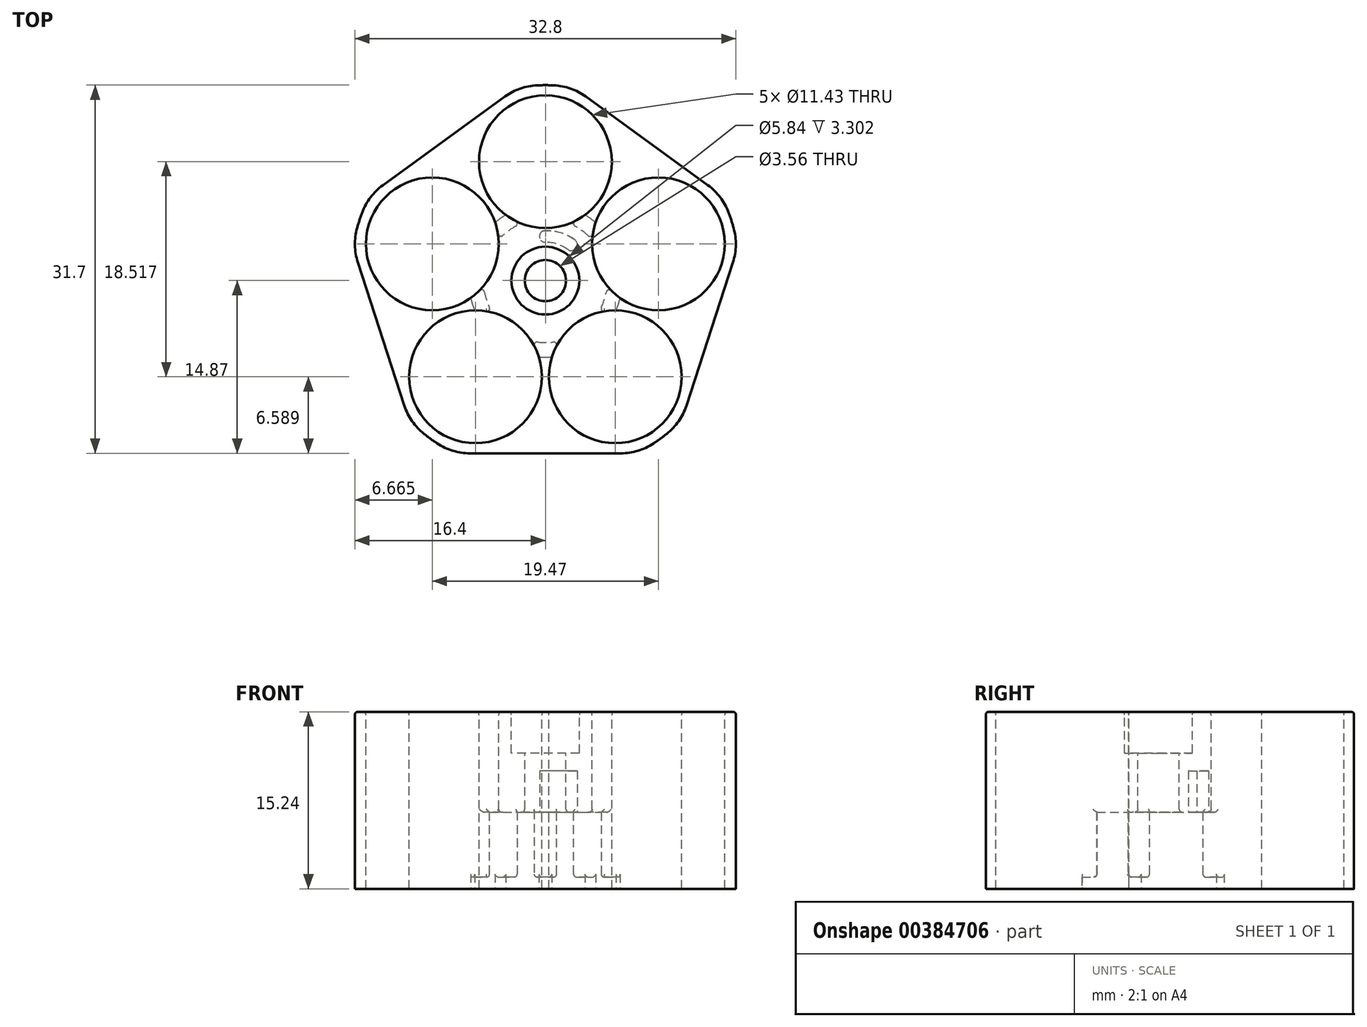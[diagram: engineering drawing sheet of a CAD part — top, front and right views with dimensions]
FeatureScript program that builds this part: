
annotation { "Feature Type Name" : "Feature", "Feature Type Description" : "" }
export const myFeature = defineFeature(function(context is Context, id is Id, definition is map)
    precondition{}
    {
        {
            var Q0;
            Q0=qCreatedBy(makeId("Top.planeOp"),FACE);
            var sketch = newSketch(context, id + "F0", { "sketchPlane" : qUnion([Q0])});
            skCircle(sketch, "E0", {"center": v(0, 0) * mm, "radius": 16.83 * mm});
            skSolve(sketch);
        }
        {
            var Q0;
            Q0=qSketchRegion(id+"F0",true);
            extrude(context, id + "F1", {"entities" : qUnion([Q0]), "depth" : 15.24 * mm, "offsetDistance" : 25.4 * mm});
        }
        {
            var Q0;
            Q0=makeQuery(id+"F1.opExtrude","CAP_FACE",FACE,{"disambiguationData":[OSD([sQuery(id+"F0.wireOp",EDGE,"E0")])],"isStart":false});
            var sketch = newSketch(context, id + "F2", { "sketchPlane" : qUnion([Q0])});
            skCircle(sketch, "E1", {"center": v(0, 10.24) * mm, "radius": 5.72 * mm});
            skCircle(sketch, "E2.1.0", {"center": v(-9.74, 3.16) * mm, "radius": 5.72 * mm});
            skCircle(sketch, "E2.2.0", {"center": v(-6.02, -8.28) * mm, "radius": 5.72 * mm});
            skCircle(sketch, "E2.3.0", {"center": v(6.02, -8.28) * mm, "radius": 5.72 * mm});
            skCircle(sketch, "E2.4.0", {"center": v(9.74, 3.16) * mm, "radius": 5.72 * mm});
            skPoint(sketch, "E2.center", {"position": v(0, 0) * mm});
            skSolve(sketch);
        }
        {
            var Q0;
            Q0=qSketchRegion(id+"F2",true);
            extrude(context, id + "F3", {"entities" : qUnion([Q0]), "operationType" : NewBodyOperationType.REMOVE, "oppositeDirection" : true, "depth" : 15.24 * mm});
        }
        {
            var Q0;
            Q0=makeQuery(id+"F1.opExtrude","CAP_FACE",FACE,{"disambiguationData":[OSD([sQuery(id+"F0.wireOp",EDGE,"E0")])],"isStart":true});
            var sketch = newSketch(context, id + "F4", { "sketchPlane" : qUnion([Q0])});
            skCircle(sketch, "E3", {"center": v(0, 0) * mm, "radius": 5.33 * mm});
            skSolve(sketch);
        }
        {
            var Q0;
            Q0=qSketchRegion(id+"F4",true);
            extrude(context, id + "F5", {"entities" : qUnion([Q0]), "operationType" : NewBodyOperationType.REMOVE, "oppositeDirection" : true, "depth" : 6.6 * mm, "offsetDistance" : 25.4 * mm});
        }
        {
            var Q0;
            Q0=makeQuery(id+"F1.opExtrude","CAP_FACE",FACE,{"disambiguationData":[OSD([sQuery(id+"F0.wireOp",EDGE,"E0")])],"isStart":false});
            var sketch = newSketch(context, id + "F6", { "sketchPlane" : qUnion([Q0])});
            skCircle(sketch, "E4", {"center": v(0, 0) * mm, "radius": 2.92 * mm});
            skSolve(sketch);
        }
        {
            var Q0;
            Q0=qSketchRegion(id+"F6",true);
            extrude(context, id + "F7", {"entities" : qUnion([Q0]), "operationType" : NewBodyOperationType.REMOVE, "oppositeDirection" : true, "depth" : 3.56 * mm});
        }
        {
            var Q0;
            Q0=makeQuery(id+"F7.boolean.opBoolean","COPY",FACE,{"derivedFrom":makeQuery(id+"F7.opExtrude","CAP_FACE",FACE,{"disambiguationData":[OSD([sQuery(id+"F6.wireOp",EDGE,"E4")])],"isStart":false})});
            var sketch = newSketch(context, id + "F8", { "sketchPlane" : qUnion([Q0])});
            skCircle(sketch, "E5", {"center": v(0, 0) * mm, "radius": 1.78 * mm});
            skSolve(sketch);
        }
        {
            var Q0;
            Q0=qSketchRegion(id+"F8",true);
            extrude(context, id + "F9", {"entities" : qUnion([Q0]), "operationType" : NewBodyOperationType.REMOVE, "oppositeDirection" : true, "depth" : 25.4 * mm});
        }
        {
            var Q0;
            Q0=makeQuery(id+"F1.opExtrude","CAP_FACE",FACE,{"disambiguationData":[OSD([sQuery(id+"F0.wireOp",EDGE,"E0")])],"isStart":true});
            var sketch = newSketch(context, id + "F10", { "sketchPlane" : qUnion([Q0])});
            skSolve(sketch);
        }
        {
            var Q0;
            {var subQ0=sQuery(id+"F0.wireOp",EDGE,"E0");Q0=makeQuery(id+"F10.imprint","IMPRINT",FACE,{"disambiguationData":[TD([[makeQuery(id+"F10.imprint","IMPRINT",EDGE,{"derivedFrom":makeQuery(id+"F1.opExtrude","CAP_EDGE",EDGE,{"disambiguationData":[OSD([subQ0])],"isStart":true})}),-1.0]])]});}
            var sketch = newSketch(context, id + "F11", { "sketchPlane" : qUnion([Q0])});
            skCircle(sketch, "E6", {"center": v(0, 0) * mm, "radius": 6.6 * mm});
            skSolve(sketch);
        }
        {
            var Q0;
            Q0=qSketchRegion(id+"F11",true);
            extrude(context, id + "F12", {"entities" : qUnion([Q0]), "operationType" : NewBodyOperationType.REMOVE, "oppositeDirection" : true, "depth" : 1.02 * mm, "offsetDistance" : 25.4 * mm});
        }
        {
            var Q0;
            Q0=qCreatedBy(makeId("Top.planeOp"),FACE);
            var sketch = newSketch(context, id + "F13", { "sketchPlane" : qUnion([Q0])});
            skArc(sketch, "E7", {"start": v(0, 4.32) * mm, "mid": v(-0.5, 3.81) * mm, "end": v(0, 3.3) * mm});
            skArc(sketch, "E8", {"start": v(1.94, 2.67) * mm, "mid": v(2.65, 2.78) * mm, "end": v(2.54, 3.5) * mm});
            skArc(sketch, "E9", {"start": v(1.94, 2.67) * mm, "mid": v(1.02, 3.14) * mm, "end": v(0, 3.3) * mm});
            skArc(sketch, "E10", {"start": v(2.54, 3.5) * mm, "mid": v(1.33, 4.1) * mm, "end": v(0, 4.32) * mm});
            skPoint(sketch, "E11.trimOffspring.end.orphan", {"position": v(6.02, -8.28) * mm});
            skSolve(sketch);
        }
        {
            var Q0;
            Q0=qSketchRegion(id+"F13",true);
            extrude(context, id + "F14", {"entities" : qUnion([Q0]), "operationType" : NewBodyOperationType.REMOVE, "depth" : 10.16 * mm, "offsetDistance" : 25.4 * mm});
        }
        {
            var Q0;
            Q0=makeQuery(id+"F5.boolean.opBoolean","INTERSECT",EDGE,{"disambiguationData":[OD(0.0)],"derivedFrom":[makeQuery(id+"F3.boolean.opBoolean","COPY",FACE,{"derivedFrom":makeQuery(id+"F3.opExtrude","SWEPT_FACE",FACE,{"disambiguationData":[OSD([sQuery(id+"F2.wireOp",EDGE,"E2.3.0")])]})}),makeQuery(id+"F5.opExtrude","SWEPT_FACE",FACE,{"disambiguationData":[OSD([sQuery(id+"F4.wireOp",EDGE,"E3")])]})]});
            var Q1;
            Q1=makeQuery(id+"F5.boolean.opBoolean","INTERSECT",EDGE,{"disambiguationData":[OD(1.0)],"derivedFrom":[makeQuery(id+"F3.boolean.opBoolean","COPY",FACE,{"derivedFrom":makeQuery(id+"F3.opExtrude","SWEPT_FACE",FACE,{"disambiguationData":[OSD([sQuery(id+"F2.wireOp",EDGE,"E2.2.0")])]})}),makeQuery(id+"F5.opExtrude","SWEPT_FACE",FACE,{"disambiguationData":[OSD([sQuery(id+"F4.wireOp",EDGE,"E3")])]})]});
            var Q2;
            Q2=makeQuery(id+"F5.boolean.opBoolean","INTERSECT",EDGE,{"disambiguationData":[OD(0.0)],"derivedFrom":[makeQuery(id+"F3.boolean.opBoolean","COPY",FACE,{"derivedFrom":makeQuery(id+"F3.opExtrude","SWEPT_FACE",FACE,{"disambiguationData":[OSD([sQuery(id+"F2.wireOp",EDGE,"E2.2.0")])]})}),makeQuery(id+"F5.opExtrude","SWEPT_FACE",FACE,{"disambiguationData":[OSD([sQuery(id+"F4.wireOp",EDGE,"E3")])]})]});
            var Q3;
            Q3=makeQuery(id+"F5.boolean.opBoolean","INTERSECT",EDGE,{"disambiguationData":[OD(1.0)],"derivedFrom":[makeQuery(id+"F3.boolean.opBoolean","COPY",FACE,{"derivedFrom":makeQuery(id+"F3.opExtrude","SWEPT_FACE",FACE,{"disambiguationData":[OSD([sQuery(id+"F2.wireOp",EDGE,"E2.1.0")])]})}),makeQuery(id+"F5.opExtrude","SWEPT_FACE",FACE,{"disambiguationData":[OSD([sQuery(id+"F4.wireOp",EDGE,"E3")])]})]});
            var Q4;
            Q4=makeQuery(id+"F5.boolean.opBoolean","INTERSECT",EDGE,{"disambiguationData":[OD(1.0)],"derivedFrom":[makeQuery(id+"F3.boolean.opBoolean","COPY",FACE,{"derivedFrom":makeQuery(id+"F3.opExtrude","SWEPT_FACE",FACE,{"disambiguationData":[OSD([sQuery(id+"F2.wireOp",EDGE,"E2.4.0")])]})}),makeQuery(id+"F5.opExtrude","SWEPT_FACE",FACE,{"disambiguationData":[OSD([sQuery(id+"F4.wireOp",EDGE,"E3")])]})]});
            var Q5;
            Q5=makeQuery(id+"F5.boolean.opBoolean","INTERSECT",EDGE,{"disambiguationData":[OD(1.0)],"derivedFrom":[makeQuery(id+"F3.boolean.opBoolean","COPY",FACE,{"derivedFrom":makeQuery(id+"F3.opExtrude","SWEPT_FACE",FACE,{"disambiguationData":[OSD([sQuery(id+"F2.wireOp",EDGE,"E2.3.0")])]})}),makeQuery(id+"F5.opExtrude","SWEPT_FACE",FACE,{"disambiguationData":[OSD([sQuery(id+"F4.wireOp",EDGE,"E3")])]})]});
            var Q6;
            Q6=makeQuery(id+"F5.boolean.opBoolean","INTERSECT",EDGE,{"disambiguationData":[OD(0.0)],"derivedFrom":[makeQuery(id+"F3.boolean.opBoolean","COPY",FACE,{"derivedFrom":makeQuery(id+"F3.opExtrude","SWEPT_FACE",FACE,{"disambiguationData":[OSD([sQuery(id+"F2.wireOp",EDGE,"E2.4.0")])]})}),makeQuery(id+"F5.opExtrude","SWEPT_FACE",FACE,{"disambiguationData":[OSD([sQuery(id+"F4.wireOp",EDGE,"E3")])]})]});
            var Q7;
            Q7=makeQuery(id+"F5.boolean.opBoolean","INTERSECT",EDGE,{"disambiguationData":[OD(1.0)],"derivedFrom":[makeQuery(id+"F3.boolean.opBoolean","COPY",FACE,{"derivedFrom":makeQuery(id+"F3.opExtrude","SWEPT_FACE",FACE,{"disambiguationData":[OSD([sQuery(id+"F2.wireOp",EDGE,"E1")])]})}),makeQuery(id+"F5.opExtrude","SWEPT_FACE",FACE,{"disambiguationData":[OSD([sQuery(id+"F4.wireOp",EDGE,"E3")])]})]});
            var Q8;
            Q8=makeQuery(id+"F5.boolean.opBoolean","INTERSECT",EDGE,{"disambiguationData":[OD(0.0)],"derivedFrom":[makeQuery(id+"F3.boolean.opBoolean","COPY",FACE,{"derivedFrom":makeQuery(id+"F3.opExtrude","SWEPT_FACE",FACE,{"disambiguationData":[OSD([sQuery(id+"F2.wireOp",EDGE,"E2.1.0")])]})}),makeQuery(id+"F5.opExtrude","SWEPT_FACE",FACE,{"disambiguationData":[OSD([sQuery(id+"F4.wireOp",EDGE,"E3")])]})]});
            var Q9;
            Q9=makeQuery(id+"F5.boolean.opBoolean","INTERSECT",EDGE,{"disambiguationData":[OD(0.0)],"derivedFrom":[makeQuery(id+"F3.boolean.opBoolean","COPY",FACE,{"derivedFrom":makeQuery(id+"F3.opExtrude","SWEPT_FACE",FACE,{"disambiguationData":[OSD([sQuery(id+"F2.wireOp",EDGE,"E1")])]})}),makeQuery(id+"F5.opExtrude","SWEPT_FACE",FACE,{"disambiguationData":[OSD([sQuery(id+"F4.wireOp",EDGE,"E3")])]})]});
            var Q10;
            Q10=makeQuery(id+"F5.boolean.opBoolean","INTERSECT",EDGE,{"derivedFrom":[makeQuery(id+"F3.boolean.opBoolean","COPY",FACE,{"derivedFrom":makeQuery(id+"F3.opExtrude","SWEPT_FACE",FACE,{"disambiguationData":[OSD([sQuery(id+"F2.wireOp",EDGE,"E2.1.0")])]})}),makeQuery(id+"F5.opExtrude","CAP_FACE",FACE,{"disambiguationData":[OSD([sQuery(id+"F4.wireOp",EDGE,"E3")])],"isStart":false})]});
            var Q11;
            Q11=makeQuery(id+"F5.boolean.opBoolean","INTERSECT",EDGE,{"derivedFrom":[makeQuery(id+"F3.boolean.opBoolean","COPY",FACE,{"derivedFrom":makeQuery(id+"F3.opExtrude","SWEPT_FACE",FACE,{"disambiguationData":[OSD([sQuery(id+"F2.wireOp",EDGE,"E2.2.0")])]})}),makeQuery(id+"F5.opExtrude","CAP_FACE",FACE,{"disambiguationData":[OSD([sQuery(id+"F4.wireOp",EDGE,"E3")])],"isStart":false})]});
            var Q12;
            Q12=makeQuery(id+"F5.boolean.opBoolean","INTERSECT",EDGE,{"derivedFrom":[makeQuery(id+"F3.boolean.opBoolean","COPY",FACE,{"derivedFrom":makeQuery(id+"F3.opExtrude","SWEPT_FACE",FACE,{"disambiguationData":[OSD([sQuery(id+"F2.wireOp",EDGE,"E2.3.0")])]})}),makeQuery(id+"F5.opExtrude","CAP_FACE",FACE,{"disambiguationData":[OSD([sQuery(id+"F4.wireOp",EDGE,"E3")])],"isStart":false})]});
            var Q13;
            Q13=makeQuery(id+"F5.boolean.opBoolean","INTERSECT",EDGE,{"derivedFrom":[makeQuery(id+"F3.boolean.opBoolean","COPY",FACE,{"derivedFrom":makeQuery(id+"F3.opExtrude","SWEPT_FACE",FACE,{"disambiguationData":[OSD([sQuery(id+"F2.wireOp",EDGE,"E2.4.0")])]})}),makeQuery(id+"F5.opExtrude","CAP_FACE",FACE,{"disambiguationData":[OSD([sQuery(id+"F4.wireOp",EDGE,"E3")])],"isStart":false})]});
            var Q14;
            Q14=makeQuery(id+"F5.boolean.opBoolean","INTERSECT",EDGE,{"derivedFrom":[makeQuery(id+"F3.boolean.opBoolean","COPY",FACE,{"derivedFrom":makeQuery(id+"F3.opExtrude","SWEPT_FACE",FACE,{"disambiguationData":[OSD([sQuery(id+"F2.wireOp",EDGE,"E1")])]})}),makeQuery(id+"F5.opExtrude","CAP_FACE",FACE,{"disambiguationData":[OSD([sQuery(id+"F4.wireOp",EDGE,"E3")])],"isStart":false})]});
            var Q15;
            Q15=makeQuery(id+"F9.boolean.opBoolean","INTERSECT",EDGE,{"derivedFrom":[makeQuery(id+"F5.boolean.opBoolean","COPY",FACE,{"derivedFrom":makeQuery(id+"F5.opExtrude","CAP_FACE",FACE,{"disambiguationData":[OSD([sQuery(id+"F4.wireOp",EDGE,"E3")])],"isStart":false})}),makeQuery(id+"F9.opExtrude","SWEPT_FACE",FACE,{"disambiguationData":[OSD([sQuery(id+"F8.wireOp",EDGE,"E5")])]})]});
            var Q16;
            Q16=makeQuery(id+"F9.boolean.opBoolean","COPY",EDGE,{"derivedFrom":makeQuery(id+"F9.opExtrude","CAP_EDGE",EDGE,{"disambiguationData":[OSD([sQuery(id+"F8.wireOp",EDGE,"E5")])],"isStart":true})});
            var Q17;
            Q17=makeQuery(id+"F12.boolean.opBoolean","INTERSECT",EDGE,{"disambiguationData":[OD(1.0)],"derivedFrom":[makeQuery(id+"F3.boolean.opBoolean","COPY",FACE,{"derivedFrom":makeQuery(id+"F3.opExtrude","SWEPT_FACE",FACE,{"disambiguationData":[OSD([sQuery(id+"F2.wireOp",EDGE,"E2.1.0")])]})}),makeQuery(id+"F12.opExtrude","CAP_FACE",FACE,{"disambiguationData":[OSD([sQuery(id+"F11.wireOp",EDGE,"E6")])],"isStart":false})]});
            var Q18;
            Q18=makeQuery(id+"F12.boolean.opBoolean","INTERSECT",EDGE,{"disambiguationData":[OD(0.0)],"derivedFrom":[makeQuery(id+"F3.boolean.opBoolean","COPY",FACE,{"derivedFrom":makeQuery(id+"F3.opExtrude","SWEPT_FACE",FACE,{"disambiguationData":[OSD([sQuery(id+"F2.wireOp",EDGE,"E2.2.0")])]})}),makeQuery(id+"F12.opExtrude","CAP_FACE",FACE,{"disambiguationData":[OSD([sQuery(id+"F11.wireOp",EDGE,"E6")])],"isStart":false})]});
            var Q19;
            {var subQ0=sQuery(id+"F4.wireOp",EDGE,"E3");Q19=makeQuery(id+"F12.boolean.opBoolean","INTERSECT",EDGE,{"derivedFrom":[makeQuery(id+"F5.boolean.opBoolean","COPY",FACE,{"disambiguationData":[TD([makeQuery(id+"F1.opExtrude","CAP_FACE",FACE,{"disambiguationData":[OSD([sQuery(id+"F0.wireOp",EDGE,"E0")])],"isStart":true}),makeQuery(id+"F3.boolean.opBoolean","COPY",FACE,{"derivedFrom":makeQuery(id+"F3.opExtrude","SWEPT_FACE",FACE,{"disambiguationData":[OSD([sQuery(id+"F2.wireOp",EDGE,"E2.1.0")])]})}),makeQuery(id+"F3.boolean.opBoolean","COPY",FACE,{"derivedFrom":makeQuery(id+"F3.opExtrude","SWEPT_FACE",FACE,{"disambiguationData":[OSD([sQuery(id+"F2.wireOp",EDGE,"E2.2.0")])]})}),makeQuery(id+"F5.opExtrude","CAP_FACE",FACE,{"disambiguationData":[OSD([subQ0])],"isStart":false})])],"derivedFrom":makeQuery(id+"F5.opExtrude","SWEPT_FACE",FACE,{"disambiguationData":[OSD([subQ0])]})}),makeQuery(id+"F12.opExtrude","CAP_FACE",FACE,{"disambiguationData":[OSD([sQuery(id+"F11.wireOp",EDGE,"E6")])],"isStart":false})]});}
            var Q20;
            Q20=makeQuery(id+"F12.boolean.opBoolean","INTERSECT",EDGE,{"disambiguationData":[OD(1.0)],"derivedFrom":[makeQuery(id+"F3.boolean.opBoolean","COPY",FACE,{"derivedFrom":makeQuery(id+"F3.opExtrude","SWEPT_FACE",FACE,{"disambiguationData":[OSD([sQuery(id+"F2.wireOp",EDGE,"E2.2.0")])]})}),makeQuery(id+"F12.opExtrude","CAP_FACE",FACE,{"disambiguationData":[OSD([sQuery(id+"F11.wireOp",EDGE,"E6")])],"isStart":false})]});
            var Q21;
            {var subQ0=sQuery(id+"F4.wireOp",EDGE,"E3");Q21=makeQuery(id+"F12.boolean.opBoolean","INTERSECT",EDGE,{"derivedFrom":[makeQuery(id+"F5.boolean.opBoolean","COPY",FACE,{"disambiguationData":[TD([makeQuery(id+"F1.opExtrude","CAP_FACE",FACE,{"disambiguationData":[OSD([sQuery(id+"F0.wireOp",EDGE,"E0")])],"isStart":true}),makeQuery(id+"F3.boolean.opBoolean","COPY",FACE,{"derivedFrom":makeQuery(id+"F3.opExtrude","SWEPT_FACE",FACE,{"disambiguationData":[OSD([sQuery(id+"F2.wireOp",EDGE,"E2.2.0")])]})}),makeQuery(id+"F3.boolean.opBoolean","COPY",FACE,{"derivedFrom":makeQuery(id+"F3.opExtrude","SWEPT_FACE",FACE,{"disambiguationData":[OSD([sQuery(id+"F2.wireOp",EDGE,"E2.3.0")])]})}),makeQuery(id+"F5.opExtrude","CAP_FACE",FACE,{"disambiguationData":[OSD([subQ0])],"isStart":false})])],"derivedFrom":makeQuery(id+"F5.opExtrude","SWEPT_FACE",FACE,{"disambiguationData":[OSD([subQ0])]})}),makeQuery(id+"F12.opExtrude","CAP_FACE",FACE,{"disambiguationData":[OSD([sQuery(id+"F11.wireOp",EDGE,"E6")])],"isStart":false})]});}
            var Q22;
            Q22=makeQuery(id+"F12.boolean.opBoolean","INTERSECT",EDGE,{"disambiguationData":[OD(0.0)],"derivedFrom":[makeQuery(id+"F3.boolean.opBoolean","COPY",FACE,{"derivedFrom":makeQuery(id+"F3.opExtrude","SWEPT_FACE",FACE,{"disambiguationData":[OSD([sQuery(id+"F2.wireOp",EDGE,"E2.3.0")])]})}),makeQuery(id+"F12.opExtrude","CAP_FACE",FACE,{"disambiguationData":[OSD([sQuery(id+"F11.wireOp",EDGE,"E6")])],"isStart":false})]});
            var Q23;
            {var subQ0=sQuery(id+"F4.wireOp",EDGE,"E3");Q23=makeQuery(id+"F12.boolean.opBoolean","INTERSECT",EDGE,{"derivedFrom":[makeQuery(id+"F5.boolean.opBoolean","COPY",FACE,{"disambiguationData":[TD([makeQuery(id+"F1.opExtrude","CAP_FACE",FACE,{"disambiguationData":[OSD([sQuery(id+"F0.wireOp",EDGE,"E0")])],"isStart":true}),makeQuery(id+"F3.boolean.opBoolean","COPY",FACE,{"derivedFrom":makeQuery(id+"F3.opExtrude","SWEPT_FACE",FACE,{"disambiguationData":[OSD([sQuery(id+"F2.wireOp",EDGE,"E2.3.0")])]})}),makeQuery(id+"F3.boolean.opBoolean","COPY",FACE,{"derivedFrom":makeQuery(id+"F3.opExtrude","SWEPT_FACE",FACE,{"disambiguationData":[OSD([sQuery(id+"F2.wireOp",EDGE,"E2.4.0")])]})}),makeQuery(id+"F5.opExtrude","CAP_FACE",FACE,{"disambiguationData":[OSD([subQ0])],"isStart":false})])],"derivedFrom":makeQuery(id+"F5.opExtrude","SWEPT_FACE",FACE,{"disambiguationData":[OSD([subQ0])]})}),makeQuery(id+"F12.opExtrude","CAP_FACE",FACE,{"disambiguationData":[OSD([sQuery(id+"F11.wireOp",EDGE,"E6")])],"isStart":false})]});}
            var Q24;
            Q24=makeQuery(id+"F12.boolean.opBoolean","INTERSECT",EDGE,{"disambiguationData":[OD(1.0)],"derivedFrom":[makeQuery(id+"F3.boolean.opBoolean","COPY",FACE,{"derivedFrom":makeQuery(id+"F3.opExtrude","SWEPT_FACE",FACE,{"disambiguationData":[OSD([sQuery(id+"F2.wireOp",EDGE,"E2.4.0")])]})}),makeQuery(id+"F12.opExtrude","CAP_FACE",FACE,{"disambiguationData":[OSD([sQuery(id+"F11.wireOp",EDGE,"E6")])],"isStart":false})]});
            var Q25;
            Q25=makeQuery(id+"F12.boolean.opBoolean","INTERSECT",EDGE,{"disambiguationData":[OD(1.0)],"derivedFrom":[makeQuery(id+"F3.boolean.opBoolean","COPY",FACE,{"derivedFrom":makeQuery(id+"F3.opExtrude","SWEPT_FACE",FACE,{"disambiguationData":[OSD([sQuery(id+"F2.wireOp",EDGE,"E2.3.0")])]})}),makeQuery(id+"F12.opExtrude","CAP_FACE",FACE,{"disambiguationData":[OSD([sQuery(id+"F11.wireOp",EDGE,"E6")])],"isStart":false})]});
            var Q26;
            Q26=makeQuery(id+"F12.boolean.opBoolean","INTERSECT",EDGE,{"disambiguationData":[OD(1.0)],"derivedFrom":[makeQuery(id+"F3.boolean.opBoolean","COPY",FACE,{"derivedFrom":makeQuery(id+"F3.opExtrude","SWEPT_FACE",FACE,{"disambiguationData":[OSD([sQuery(id+"F2.wireOp",EDGE,"E1")])]})}),makeQuery(id+"F12.opExtrude","CAP_FACE",FACE,{"disambiguationData":[OSD([sQuery(id+"F11.wireOp",EDGE,"E6")])],"isStart":false})]});
            var Q27;
            {var subQ0=sQuery(id+"F4.wireOp",EDGE,"E3");Q27=makeQuery(id+"F12.boolean.opBoolean","INTERSECT",EDGE,{"derivedFrom":[makeQuery(id+"F5.boolean.opBoolean","COPY",FACE,{"disambiguationData":[TD([makeQuery(id+"F1.opExtrude","CAP_FACE",FACE,{"disambiguationData":[OSD([sQuery(id+"F0.wireOp",EDGE,"E0")])],"isStart":true}),makeQuery(id+"F3.boolean.opBoolean","COPY",FACE,{"derivedFrom":makeQuery(id+"F3.opExtrude","SWEPT_FACE",FACE,{"disambiguationData":[OSD([sQuery(id+"F2.wireOp",EDGE,"E1")])]})}),makeQuery(id+"F3.boolean.opBoolean","COPY",FACE,{"derivedFrom":makeQuery(id+"F3.opExtrude","SWEPT_FACE",FACE,{"disambiguationData":[OSD([sQuery(id+"F2.wireOp",EDGE,"E2.4.0")])]})}),makeQuery(id+"F5.opExtrude","CAP_FACE",FACE,{"disambiguationData":[OSD([subQ0])],"isStart":false})])],"derivedFrom":makeQuery(id+"F5.opExtrude","SWEPT_FACE",FACE,{"disambiguationData":[OSD([subQ0])]})}),makeQuery(id+"F12.opExtrude","CAP_FACE",FACE,{"disambiguationData":[OSD([sQuery(id+"F11.wireOp",EDGE,"E6")])],"isStart":false})]});}
            var Q28;
            Q28=makeQuery(id+"F12.boolean.opBoolean","INTERSECT",EDGE,{"disambiguationData":[OD(0.0)],"derivedFrom":[makeQuery(id+"F3.boolean.opBoolean","COPY",FACE,{"derivedFrom":makeQuery(id+"F3.opExtrude","SWEPT_FACE",FACE,{"disambiguationData":[OSD([sQuery(id+"F2.wireOp",EDGE,"E2.4.0")])]})}),makeQuery(id+"F12.opExtrude","CAP_FACE",FACE,{"disambiguationData":[OSD([sQuery(id+"F11.wireOp",EDGE,"E6")])],"isStart":false})]});
            var Q29;
            Q29=makeQuery(id+"F12.boolean.opBoolean","INTERSECT",EDGE,{"disambiguationData":[OD(0.0)],"derivedFrom":[makeQuery(id+"F3.boolean.opBoolean","COPY",FACE,{"derivedFrom":makeQuery(id+"F3.opExtrude","SWEPT_FACE",FACE,{"disambiguationData":[OSD([sQuery(id+"F2.wireOp",EDGE,"E2.1.0")])]})}),makeQuery(id+"F12.opExtrude","CAP_FACE",FACE,{"disambiguationData":[OSD([sQuery(id+"F11.wireOp",EDGE,"E6")])],"isStart":false})]});
            var Q30;
            {var subQ0=sQuery(id+"F4.wireOp",EDGE,"E3");Q30=makeQuery(id+"F12.boolean.opBoolean","INTERSECT",EDGE,{"derivedFrom":[makeQuery(id+"F5.boolean.opBoolean","COPY",FACE,{"disambiguationData":[TD([makeQuery(id+"F1.opExtrude","CAP_FACE",FACE,{"disambiguationData":[OSD([sQuery(id+"F0.wireOp",EDGE,"E0")])],"isStart":true}),makeQuery(id+"F3.boolean.opBoolean","COPY",FACE,{"derivedFrom":makeQuery(id+"F3.opExtrude","SWEPT_FACE",FACE,{"disambiguationData":[OSD([sQuery(id+"F2.wireOp",EDGE,"E1")])]})}),makeQuery(id+"F3.boolean.opBoolean","COPY",FACE,{"derivedFrom":makeQuery(id+"F3.opExtrude","SWEPT_FACE",FACE,{"disambiguationData":[OSD([sQuery(id+"F2.wireOp",EDGE,"E2.1.0")])]})}),makeQuery(id+"F5.opExtrude","CAP_FACE",FACE,{"disambiguationData":[OSD([subQ0])],"isStart":false})])],"derivedFrom":makeQuery(id+"F5.opExtrude","SWEPT_FACE",FACE,{"disambiguationData":[OSD([subQ0])]})}),makeQuery(id+"F12.opExtrude","CAP_FACE",FACE,{"disambiguationData":[OSD([sQuery(id+"F11.wireOp",EDGE,"E6")])],"isStart":false})]});}
            var Q31;
            Q31=makeQuery(id+"F12.boolean.opBoolean","INTERSECT",EDGE,{"disambiguationData":[OD(0.0)],"derivedFrom":[makeQuery(id+"F3.boolean.opBoolean","COPY",FACE,{"derivedFrom":makeQuery(id+"F3.opExtrude","SWEPT_FACE",FACE,{"disambiguationData":[OSD([sQuery(id+"F2.wireOp",EDGE,"E1")])]})}),makeQuery(id+"F12.opExtrude","CAP_FACE",FACE,{"disambiguationData":[OSD([sQuery(id+"F11.wireOp",EDGE,"E6")])],"isStart":false})]});
            fillet(context, id + "F15", {"entities" : qUnion([Q0, Q1, Q2, Q3, Q4, Q5, Q6, Q7, Q8, Q9, Q10, Q11, Q12, Q13, Q14, Q15, Q16, Q17, Q18, Q19, Q20, Q21, Q22, Q23, Q24, Q25, Q26, Q27, Q28, Q29, Q30, Q31]), "radius" : 0.25 * mm, "tangentPropagation" : true, "allowEdgeOverflow" : false});
        }
        {
            var Q0;
            {var subQ0=sQuery(id+"F0.wireOp",EDGE,"E0");Q0=makeQuery(id+"F10.imprint","IMPRINT",FACE,{"disambiguationData":[TD([[makeQuery(id+"F10.imprint","IMPRINT",EDGE,{"derivedFrom":makeQuery(id+"F1.opExtrude","CAP_EDGE",EDGE,{"disambiguationData":[OSD([subQ0])],"isStart":true})}),-1.0]])]});}
            var sketch = newSketch(context, id + "F16", { "sketchPlane" : qUnion([Q0])});
            skLineSegment(sketch, "E12.bottom", {"start": v(-14.26, 20.97) * mm, "end": v(14.42, 20.97) * mm});
            skLineSegment(sketch, "E12.top", {"start": v(-14.26, 14.87) * mm, "end": v(14.42, 14.87) * mm});
            skLineSegment(sketch, "E12.left", {"start": v(-14.26, 20.97) * mm, "end": v(-14.26, 14.87) * mm});
            skLineSegment(sketch, "E12.right", {"start": v(14.42, 20.97) * mm, "end": v(14.42, 14.87) * mm});
            skLineSegment(sketch, "E13.1.0", {"start": v(-24.35, -7.08) * mm, "end": v(-15.49, 20.2) * mm});
            skLineSegment(sketch, "E13.1.1", {"start": v(-18.55, -8.97) * mm, "end": v(-9.68, 18.31) * mm});
            skLineSegment(sketch, "E13.1.2", {"start": v(-24.35, -7.08) * mm, "end": v(-18.55, -8.97) * mm});
            skLineSegment(sketch, "E13.1.3", {"start": v(-15.49, 20.2) * mm, "end": v(-9.68, 18.31) * mm});
            skLineSegment(sketch, "E13.2.0", {"start": v(-0.8, -25.34) * mm, "end": v(-24, -8.49) * mm});
            skLineSegment(sketch, "E13.2.1", {"start": v(2.8, -20.4) * mm, "end": v(-20.4, -3.55) * mm});
            skLineSegment(sketch, "E13.2.2", {"start": v(-0.8, -25.34) * mm, "end": v(2.8, -20.4) * mm});
            skLineSegment(sketch, "E13.2.3", {"start": v(-24, -8.49) * mm, "end": v(-20.4, -3.55) * mm});
            skLineSegment(sketch, "E13.3.0", {"start": v(23.86, -8.58) * mm, "end": v(0.66, -25.44) * mm});
            skLineSegment(sketch, "E13.3.1", {"start": v(20.27, -3.65) * mm, "end": v(-2.93, -20.5) * mm});
            skLineSegment(sketch, "E13.3.2", {"start": v(23.86, -8.58) * mm, "end": v(20.27, -3.65) * mm});
            skLineSegment(sketch, "E13.3.3", {"start": v(0.66, -25.44) * mm, "end": v(-2.93, -20.5) * mm});
            skLineSegment(sketch, "E13.4.0", {"start": v(15.54, 20.04) * mm, "end": v(24.4, -7.24) * mm});
            skLineSegment(sketch, "E13.4.1", {"start": v(9.73, 18.15) * mm, "end": v(18.6, -9.12) * mm});
            skLineSegment(sketch, "E13.4.2", {"start": v(15.54, 20.04) * mm, "end": v(9.73, 18.15) * mm});
            skLineSegment(sketch, "E13.4.3", {"start": v(24.4, -7.24) * mm, "end": v(18.6, -9.12) * mm});
            skPoint(sketch, "E13.center", {"position": v(0, 0) * mm});
            skSolve(sketch);
        }
        {
            var Q0;
            Q0 = qSketchRegion(id + "F16", true);
            extrude(context, id + "F17", {"entities" : qUnion([Q0]), "operationType" : NewBodyOperationType.REMOVE, "endBound" : BoundingType.THROUGH_ALL, "oppositeDirection" : true, "depth" : 25.4 * mm, "offsetDistance" : 25.4 * mm});
        }
        {
            var Q0;
            Q0=makeQuery(id+"F17.boolean.opBoolean","INTERSECT",EDGE,{"disambiguationData":[OD(1.0)],"derivedFrom":[makeQuery(id+"F1.opExtrude","SWEPT_FACE",FACE,{"disambiguationData":[OSD([sQuery(id+"F0.wireOp",EDGE,"E0")])]}),makeQuery(id+"F17.opExtrude","SWEPT_FACE",FACE,{"disambiguationData":[OSD([sQuery(id+"F16.wireOp",EDGE,"E13.1.1")])]})]});
            var Q1;
            Q1=makeQuery(id+"F17.boolean.opBoolean","INTERSECT",EDGE,{"disambiguationData":[OD(0.0)],"derivedFrom":[makeQuery(id+"F1.opExtrude","SWEPT_FACE",FACE,{"disambiguationData":[OSD([sQuery(id+"F0.wireOp",EDGE,"E0")])]}),makeQuery(id+"F17.opExtrude","SWEPT_FACE",FACE,{"disambiguationData":[OSD([sQuery(id+"F16.wireOp",EDGE,"E13.2.1")])]})]});
            var Q2;
            Q2=makeQuery(id+"F17.boolean.opBoolean","INTERSECT",EDGE,{"disambiguationData":[OD(1.0)],"derivedFrom":[makeQuery(id+"F1.opExtrude","SWEPT_FACE",FACE,{"disambiguationData":[OSD([sQuery(id+"F0.wireOp",EDGE,"E0")])]}),makeQuery(id+"F17.opExtrude","SWEPT_FACE",FACE,{"disambiguationData":[OSD([sQuery(id+"F16.wireOp",EDGE,"E13.2.1")])]})]});
            var Q3;
            Q3=makeQuery(id+"F17.boolean.opBoolean","INTERSECT",EDGE,{"disambiguationData":[OD(0.0)],"derivedFrom":[makeQuery(id+"F1.opExtrude","SWEPT_FACE",FACE,{"disambiguationData":[OSD([sQuery(id+"F0.wireOp",EDGE,"E0")])]}),makeQuery(id+"F17.opExtrude","SWEPT_FACE",FACE,{"disambiguationData":[OSD([sQuery(id+"F16.wireOp",EDGE,"E13.3.1")])]})]});
            var Q4;
            Q4=makeQuery(id+"F17.boolean.opBoolean","INTERSECT",EDGE,{"disambiguationData":[OD(1.0)],"derivedFrom":[makeQuery(id+"F1.opExtrude","SWEPT_FACE",FACE,{"disambiguationData":[OSD([sQuery(id+"F0.wireOp",EDGE,"E0")])]}),makeQuery(id+"F17.opExtrude","SWEPT_FACE",FACE,{"disambiguationData":[OSD([sQuery(id+"F16.wireOp",EDGE,"E13.3.1")])]})]});
            var Q5;
            Q5=makeQuery(id+"F17.boolean.opBoolean","INTERSECT",EDGE,{"disambiguationData":[OD(1.0)],"derivedFrom":[makeQuery(id+"F1.opExtrude","SWEPT_FACE",FACE,{"disambiguationData":[OSD([sQuery(id+"F0.wireOp",EDGE,"E0")])]}),makeQuery(id+"F17.opExtrude","SWEPT_FACE",FACE,{"disambiguationData":[OSD([sQuery(id+"F16.wireOp",EDGE,"E13.4.1")])]})]});
            var Q6;
            Q6=makeQuery(id+"F17.boolean.opBoolean","INTERSECT",EDGE,{"disambiguationData":[OD(0.0)],"derivedFrom":[makeQuery(id+"F1.opExtrude","SWEPT_FACE",FACE,{"disambiguationData":[OSD([sQuery(id+"F0.wireOp",EDGE,"E0")])]}),makeQuery(id+"F17.opExtrude","SWEPT_FACE",FACE,{"disambiguationData":[OSD([sQuery(id+"F16.wireOp",EDGE,"E13.4.1")])]})]});
            var Q7;
            Q7=makeQuery(id+"F17.boolean.opBoolean","INTERSECT",EDGE,{"disambiguationData":[OD(1.0)],"derivedFrom":[makeQuery(id+"F1.opExtrude","SWEPT_FACE",FACE,{"disambiguationData":[OSD([sQuery(id+"F0.wireOp",EDGE,"E0")])]}),makeQuery(id+"F17.opExtrude","SWEPT_FACE",FACE,{"disambiguationData":[OSD([sQuery(id+"F16.wireOp",EDGE,"E12.top")])]})]});
            var Q8;
            Q8=makeQuery(id+"F17.boolean.opBoolean","INTERSECT",EDGE,{"disambiguationData":[OD(0.0)],"derivedFrom":[makeQuery(id+"F1.opExtrude","SWEPT_FACE",FACE,{"disambiguationData":[OSD([sQuery(id+"F0.wireOp",EDGE,"E0")])]}),makeQuery(id+"F17.opExtrude","SWEPT_FACE",FACE,{"disambiguationData":[OSD([sQuery(id+"F16.wireOp",EDGE,"E12.top")])]})]});
            var Q9;
            Q9=makeQuery(id+"F17.boolean.opBoolean","INTERSECT",EDGE,{"disambiguationData":[OD(0.0)],"derivedFrom":[makeQuery(id+"F1.opExtrude","SWEPT_FACE",FACE,{"disambiguationData":[OSD([sQuery(id+"F0.wireOp",EDGE,"E0")])]}),makeQuery(id+"F17.opExtrude","SWEPT_FACE",FACE,{"disambiguationData":[OSD([sQuery(id+"F16.wireOp",EDGE,"E13.1.1")])]})]});
            fillet(context, id + "F18", {"entities" : qUnion([Q0, Q1, Q2, Q3, Q4, Q5, Q6, Q7, Q8, Q9]), "radius" : 5.08 * mm, "tangentPropagation" : true, "allowEdgeOverflow" : false});
        }
        {
            var Q0;
            Q0=makeQuery(id+"F1.opExtrude","CAP_FACE",FACE,{"disambiguationData":[OSD([sQuery(id+"F0.wireOp",EDGE,"E0")])],"isStart":false});
            var Q1;
            Q1=makeQuery(id+"F17.boolean.opBoolean","COPY",EDGE,{"derivedFrom":makeQuery(id+"F17.opExtrude","CAP_EDGE",EDGE,{"disambiguationData":[OSD([sQuery(id+"F16.wireOp",EDGE,"E12.top")])],"isStart":true})});
            var Q2;
            Q2=makeQuery(id+"F3.boolean.opBoolean","COPY",EDGE,{"derivedFrom":makeQuery(id+"F3.opExtrude","CAP_EDGE",EDGE,{"disambiguationData":[OSD([sQuery(id+"F2.wireOp",EDGE,"E2.2.0")])],"isStart":false})});
            var Q3;
            Q3=makeQuery(id+"F3.boolean.opBoolean","COPY",EDGE,{"derivedFrom":makeQuery(id+"F3.opExtrude","CAP_EDGE",EDGE,{"disambiguationData":[OSD([sQuery(id+"F2.wireOp",EDGE,"E2.3.0")])],"isStart":false})});
            var Q4;
            Q4=makeQuery(id+"F3.boolean.opBoolean","COPY",EDGE,{"derivedFrom":makeQuery(id+"F3.opExtrude","CAP_EDGE",EDGE,{"disambiguationData":[OSD([sQuery(id+"F2.wireOp",EDGE,"E2.4.0")])],"isStart":false})});
            var Q5;
            Q5=makeQuery(id+"F3.boolean.opBoolean","COPY",EDGE,{"derivedFrom":makeQuery(id+"F3.opExtrude","CAP_EDGE",EDGE,{"disambiguationData":[OSD([sQuery(id+"F2.wireOp",EDGE,"E1")])],"isStart":false})});
            var Q6;
            Q6=makeQuery(id+"F3.boolean.opBoolean","COPY",EDGE,{"derivedFrom":makeQuery(id+"F3.opExtrude","CAP_EDGE",EDGE,{"disambiguationData":[OSD([sQuery(id+"F2.wireOp",EDGE,"E2.1.0")])],"isStart":false})});
            fillet(context, id + "F19", {"entities" : qUnion([Q0, Q1, Q2, Q3, Q4, Q5, Q6]), "radius" : 0.25 * mm, "tangentPropagation" : true, "allowEdgeOverflow" : false});
        }
    });
